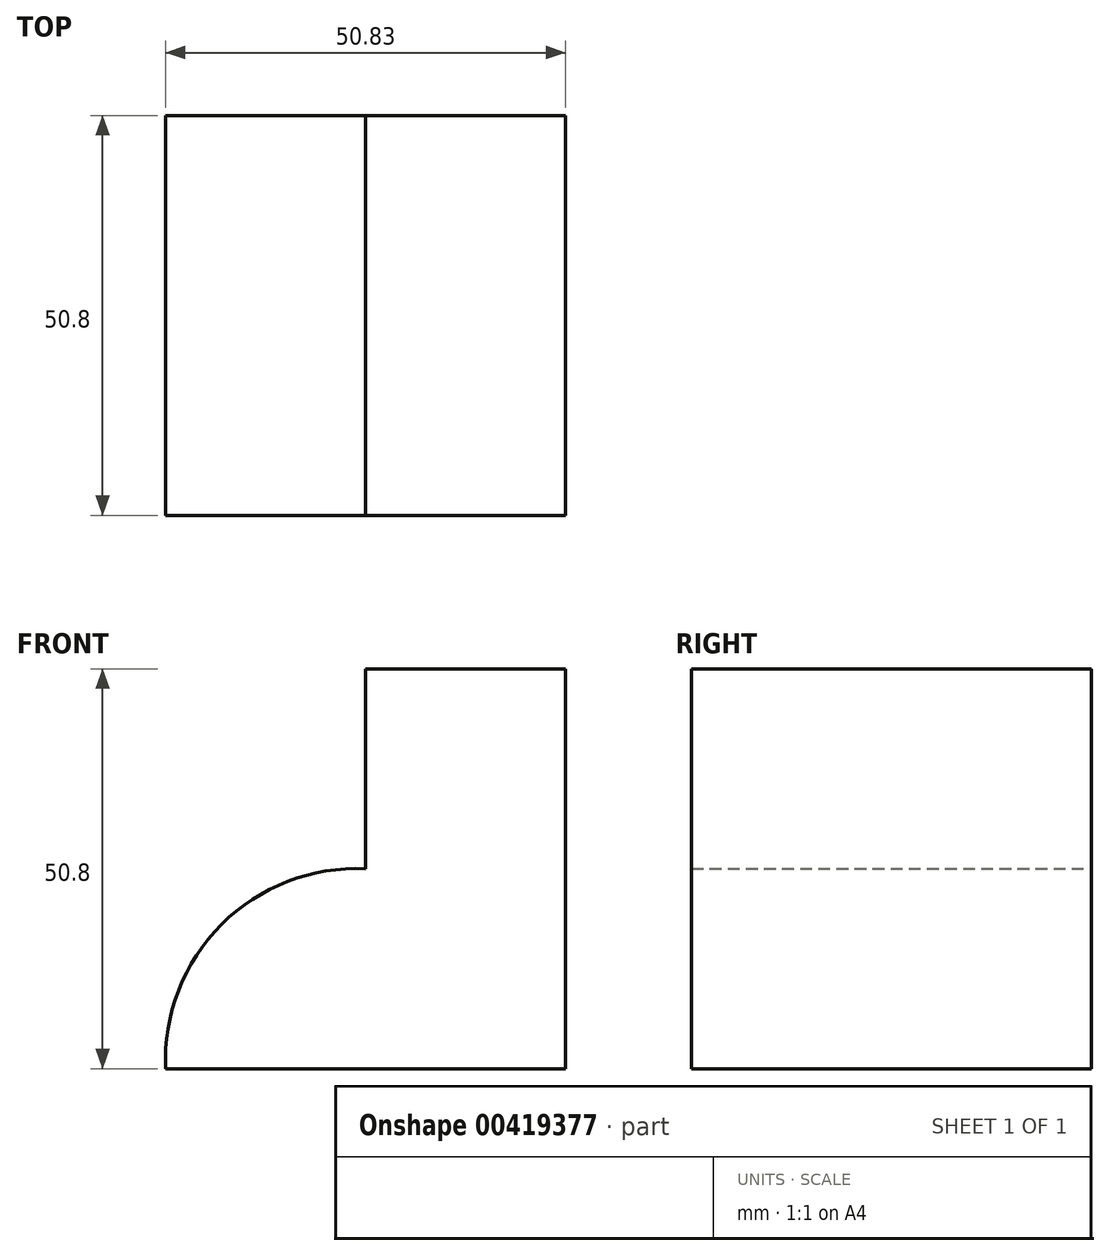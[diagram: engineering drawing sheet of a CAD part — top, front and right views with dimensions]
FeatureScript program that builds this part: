
annotation { "Feature Type Name" : "Feature", "Feature Type Description" : "" }
export const myFeature = defineFeature(function(context is Context, id is Id, definition is map)
    precondition{}
    {
        {
            var Q0;
            Q0=qCreatedBy(makeId("Front.planeOp"),FACE);
            var sketch = newSketch(context, id + "F0", { "sketchPlane" : qUnion([Q0])});
            skLineSegment(sketch, "E0", {"start": v(0, 0) * mm, "end": v(50.8, 0) * mm});
            skLineSegment(sketch, "E1", {"start": v(50.8, 0) * mm, "end": v(50.8, 50.8) * mm});
            skLineSegment(sketch, "E2", {"start": v(50.8, 50.8) * mm, "end": v(25.4, 50.8) * mm});
            skLineSegment(sketch, "E3", {"start": v(25.4, 50.8) * mm, "end": v(25.4, 25.4) * mm});
            skArc(sketch, "E4", {"start": v(25.4, 25.4) * mm, "mid": v(7.09, 18.31) * mm, "end": v(0, 0) * mm});
            skSolve(sketch);
        }
        {
            var Q0;
            Q0 = qSketchRegion(id + "F0", true);
            extrude(context, id + "F1", {"entities" : qUnion([Q0]), "depth" : 50.8 * mm});
        }
    });
